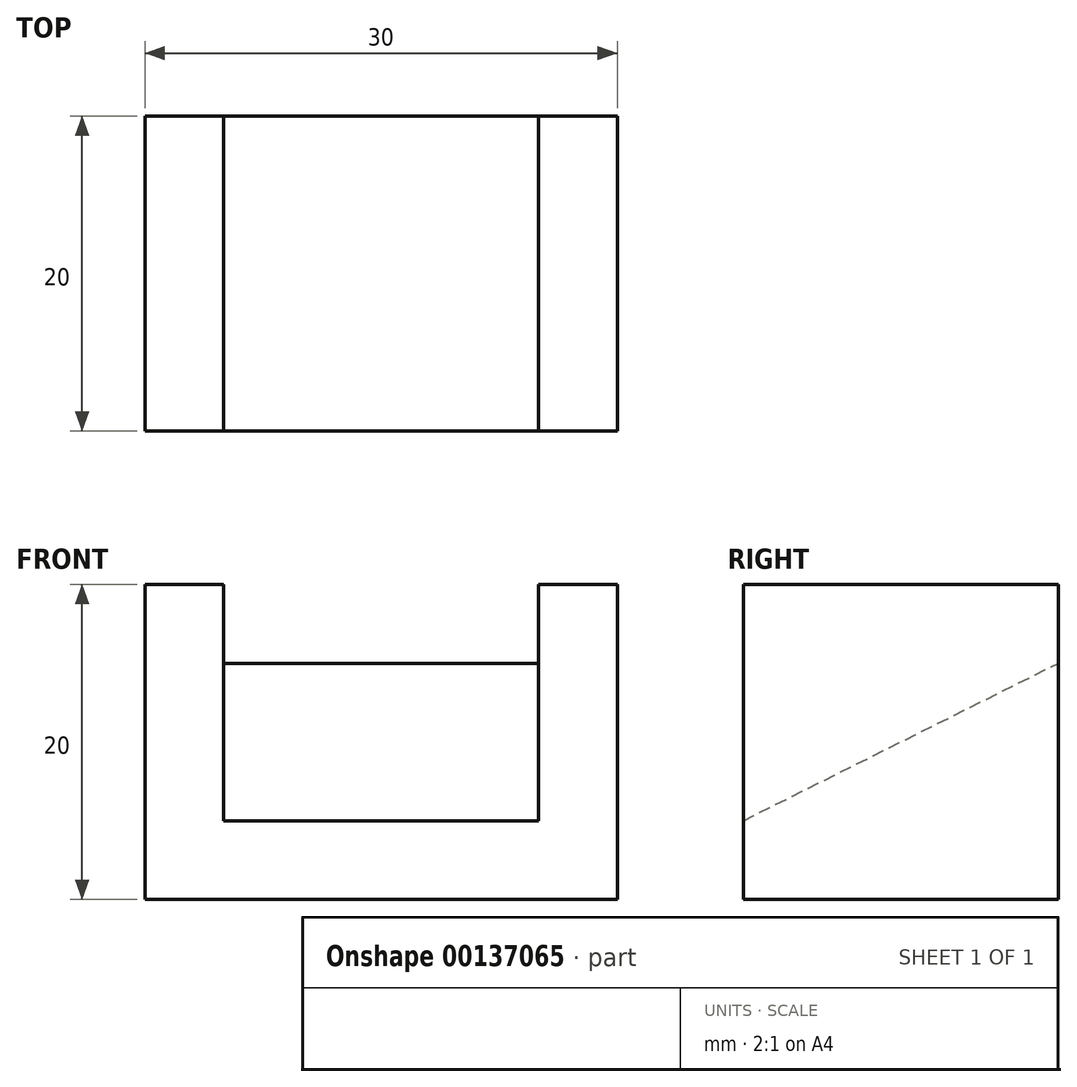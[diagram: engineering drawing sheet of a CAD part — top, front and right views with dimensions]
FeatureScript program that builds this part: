
annotation { "Feature Type Name" : "Feature", "Feature Type Description" : "" }
export const myFeature = defineFeature(function(context is Context, id is Id, definition is map)
    precondition{}
    {
        {
            var Q0;
            Q0=qCreatedBy(makeId("Front.planeOp"),FACE);
            var sketch = newSketch(context, id + "F0", { "sketchPlane" : qUnion([Q0])});
            skLineSegment(sketch, "E0", {"start": v(0, 0) * mm, "end": v(25, 0) * mm});
            skLineSegment(sketch, "E1", {"start": v(25, 0) * mm, "end": v(25, 20) * mm});
            skLineSegment(sketch, "E2", {"start": v(25, 20) * mm, "end": v(0, 20) * mm});
            skLineSegment(sketch, "E3", {"start": v(0, 20) * mm, "end": v(0, 0) * mm});
            skSolve(sketch);
        }
        {
            var Q0;
            Q0 = qSketchRegion(id + "F0", true);
            extrude(context, id + "F1", {"entities" : qUnion([Q0]), "oppositeDirection" : true, "depth" : 20 * mm});
        }
        {
            var Q0;
            Q0=makeQuery(id+"F1.opExtrude","SWEPT_FACE",FACE,{"disambiguationData":[OSD([sQuery(id+"F0.wireOp",EDGE,"E1")])]});
            var sketch = newSketch(context, id + "F2", { "sketchPlane" : qUnion([Q0])});
            skLineSegment(sketch, "E4", {"start": v(0, 5) * mm, "end": v(20, 15) * mm});
            skLineSegment(sketch, "E5", {"start": v(20, 15) * mm, "end": v(20, 20) * mm});
            skLineSegment(sketch, "E6", {"start": v(20, 20) * mm, "end": v(0, 20) * mm});
            skLineSegment(sketch, "E7", {"start": v(0, 20) * mm, "end": v(0, 5) * mm});
            skSolve(sketch);
        }
        {
            var Q0;
            Q0 = qSketchRegion(id + "F2", true);
            extrude(context, id + "F3", {"entities" : qUnion([Q0]), "operationType" : NewBodyOperationType.REMOVE, "oppositeDirection" : true, "depth" : 20 * mm});
        }
        {
            var Q0;
            Q0=makeQuery(id+"F1.opExtrude","SWEPT_FACE",FACE,{"disambiguationData":[OSD([sQuery(id+"F0.wireOp",EDGE,"E1")])]});
            var sketch = newSketch(context, id + "F4", { "sketchPlane" : qUnion([Q0])});
            skLineSegment(sketch, "E8.bottom", {"start": v(0, 0) * mm, "end": v(20, 0) * mm});
            skLineSegment(sketch, "E8.top", {"start": v(0, 20) * mm, "end": v(20, 20) * mm});
            skLineSegment(sketch, "E8.left", {"start": v(0, 0) * mm, "end": v(0, 20) * mm});
            skLineSegment(sketch, "E8.right", {"start": v(20, 0) * mm, "end": v(20, 20) * mm});
            skSolve(sketch);
        }
        {
            var Q0;
            Q0 = qSketchRegion(id + "F4", true);
            extrude(context, id + "F5", {"entities" : qUnion([Q0]), "operationType" : NewBodyOperationType.ADD, "depth" : 5 * mm});
        }
    });
